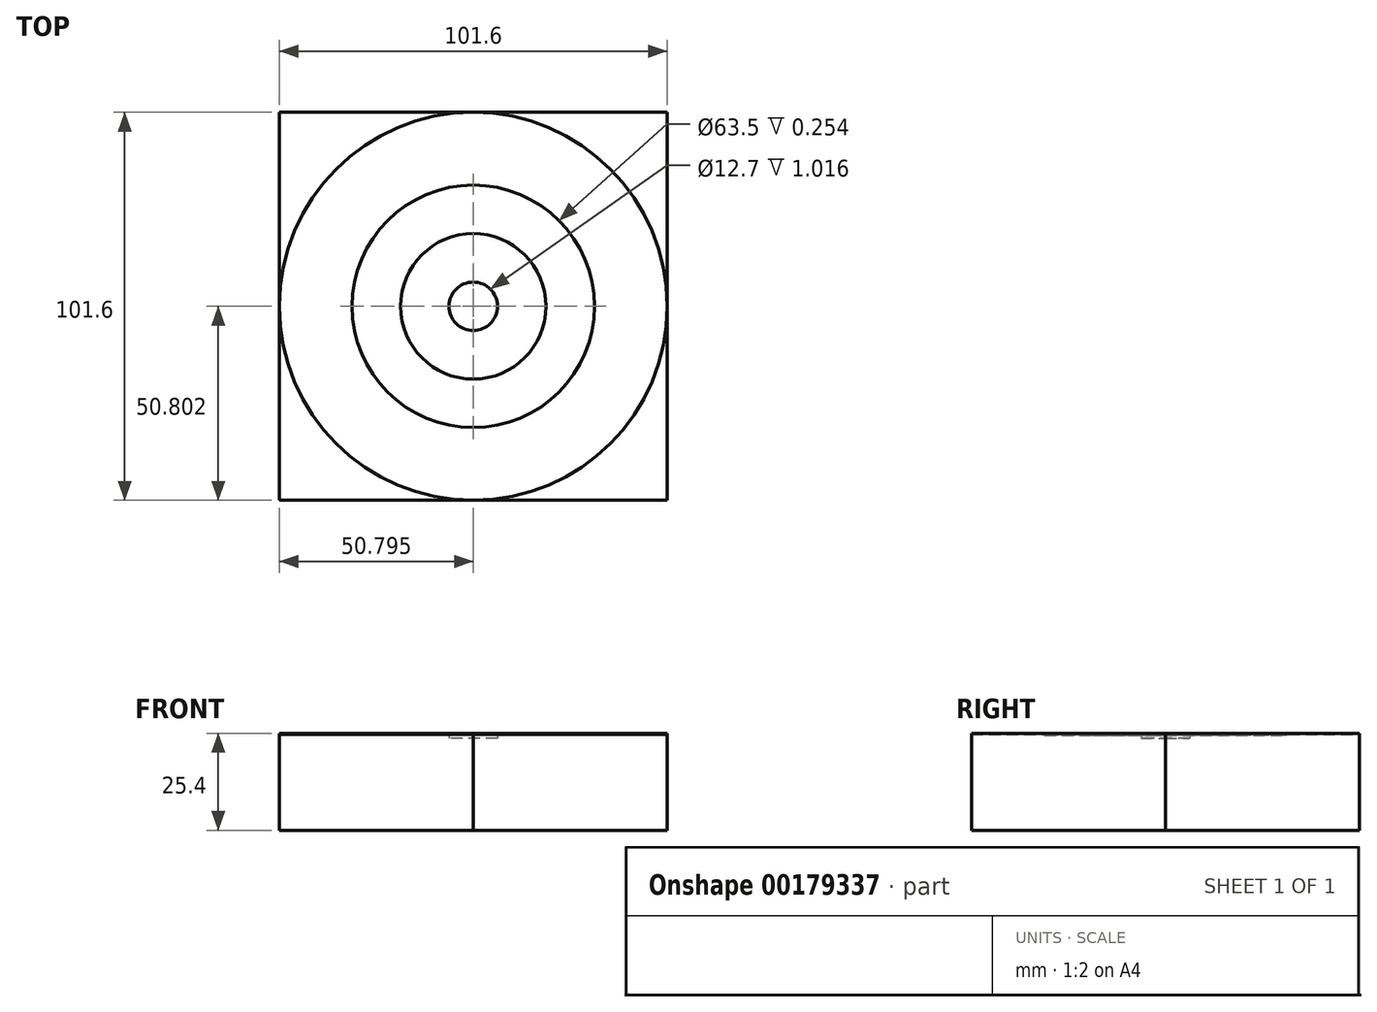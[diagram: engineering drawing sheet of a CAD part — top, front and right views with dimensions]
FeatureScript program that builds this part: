
annotation { "Feature Type Name" : "Feature", "Feature Type Description" : "" }
export const myFeature = defineFeature(function(context is Context, id is Id, definition is map)
    precondition{}
    {
        {
            var Q0;
            Q0=qCreatedBy(makeId("Top.planeOp"),FACE);
            var sketch = newSketch(context, id + "F0", { "sketchPlane" : qUnion([Q0])});
            skLineSegment(sketch, "E0.bottom", {"start": v(49.43, -40.05) * mm, "end": v(-52.17, -40.05) * mm});
            skLineSegment(sketch, "E0.top", {"start": v(49.43, 61.55) * mm, "end": v(-52.17, 61.55) * mm});
            skLineSegment(sketch, "E0.left", {"start": v(49.43, -40.05) * mm, "end": v(49.43, 61.55) * mm});
            skLineSegment(sketch, "E0.right", {"start": v(-52.17, -40.05) * mm, "end": v(-52.17, 61.55) * mm});
            skPoint(sketch, "E0.middle", {"position": v(-1.37, 10.75) * mm});
            skCircle(sketch, "E1", {"center": v(-1.37, 10.75) * mm, "radius": 50.8 * mm});
            skCircle(sketch, "E2", {"center": v(-1.37, 10.75) * mm, "radius": 31.75 * mm});
            skCircle(sketch, "E3", {"center": v(-1.37, 10.75) * mm, "radius": 19.05 * mm});
            skCircle(sketch, "E4", {"center": v(-1.37, 10.75) * mm, "radius": 6.35 * mm});
            skSolve(sketch);
        }
        {
            var Q0;
            {var subQ0=sQuery(id+"F0.wireOp",EDGE,"E0.right");var subQ1=sQuery(id+"F0.wireOp",EDGE,"E0.top");var subQ2=makeQuery(id+"F0.imprint","INTERSECT",VERTEX,{"derivedFrom":[subQ1,subQ0]});Q0=makeQuery(id+"F0.imprint","IMPRINT",FACE,{"disambiguationData":[TD([[makeQuery(id+"F0.imprint","IMPRINT",EDGE,{"disambiguationData":[TD([[subQ2,1.0]])],"derivedFrom":subQ1}),1.0]])]});}
            var Q1;
            {var subQ0=sQuery(id+"F0.wireOp",EDGE,"E0.left");var subQ1=sQuery(id+"F0.wireOp",EDGE,"E0.top");var subQ2=makeQuery(id+"F0.imprint","INTERSECT",VERTEX,{"derivedFrom":[subQ1,subQ0]});Q1=makeQuery(id+"F0.imprint","IMPRINT",FACE,{"disambiguationData":[TD([[makeQuery(id+"F0.imprint","IMPRINT",EDGE,{"disambiguationData":[TD([[subQ2,-1.0]])],"derivedFrom":subQ1}),1.0]])]});}
            var Q2;
            {var subQ0=sQuery(id+"F0.wireOp",EDGE,"E0.left");var subQ1=sQuery(id+"F0.wireOp",EDGE,"E0.bottom");var subQ2=makeQuery(id+"F0.imprint","INTERSECT",VERTEX,{"derivedFrom":[subQ1,subQ0]});Q2=makeQuery(id+"F0.imprint","IMPRINT",FACE,{"disambiguationData":[TD([[makeQuery(id+"F0.imprint","IMPRINT",EDGE,{"disambiguationData":[TD([[subQ2,-1.0]])],"derivedFrom":subQ1}),-1.0]])]});}
            var Q3;
            {var subQ0=sQuery(id+"F0.wireOp",EDGE,"E0.right");var subQ1=sQuery(id+"F0.wireOp",EDGE,"E0.bottom");var subQ2=makeQuery(id+"F0.imprint","INTERSECT",VERTEX,{"derivedFrom":[subQ1,subQ0]});Q3=makeQuery(id+"F0.imprint","IMPRINT",FACE,{"disambiguationData":[TD([[makeQuery(id+"F0.imprint","IMPRINT",EDGE,{"disambiguationData":[TD([[subQ2,1.0]])],"derivedFrom":subQ1}),-1.0]])]});}
            extrude(context, id + "F1", {"entities" : qUnion([Q0, Q1, Q2, Q3]), "depth" : 25.4 * mm});
        }
        {
            var Q0;
            Q0=makeQuery(id+"F0.imprint","IMPRINT",FACE,{"disambiguationData":[TD([[makeQuery(id+"F0.imprint","IMPRINT",EDGE,{"derivedFrom":sQuery(id+"F0.wireOp",EDGE,"E2")}),-1.0]])]});
            extrude(context, id + "F2", {"entities" : qUnion([Q0]), "depth" : 25.15 * mm});
        }
        {
            var Q0;
            Q0=makeQuery(id+"F0.imprint","IMPRINT",FACE,{"disambiguationData":[TD([[makeQuery(id+"F0.imprint","IMPRINT",EDGE,{"derivedFrom":sQuery(id+"F0.wireOp",EDGE,"E2")}),1.0]])]});
            extrude(context, id + "F3", {"entities" : qUnion([Q0]), "operationType" : NewBodyOperationType.ADD, "depth" : 24.9 * mm});
        }
        {
            var Q0;
            Q0=makeQuery(id+"F0.imprint","IMPRINT",FACE,{"disambiguationData":[TD([[makeQuery(id+"F0.imprint","IMPRINT",EDGE,{"derivedFrom":sQuery(id+"F0.wireOp",EDGE,"E3")}),1.0]])]});
            extrude(context, id + "F4", {"entities" : qUnion([Q0]), "operationType" : NewBodyOperationType.ADD, "depth" : 25.15 * mm});
        }
        {
            var Q0;
            Q0=makeQuery(id+"F0.imprint","IMPRINT",FACE,{"disambiguationData":[TD([[makeQuery(id+"F0.imprint","IMPRINT",EDGE,{"derivedFrom":sQuery(id+"F0.wireOp",EDGE,"E4")}),1.0]])]});
            extrude(context, id + "F5", {"entities" : qUnion([Q0]), "operationType" : NewBodyOperationType.ADD, "depth" : 24.13 * mm});
        }
    });
